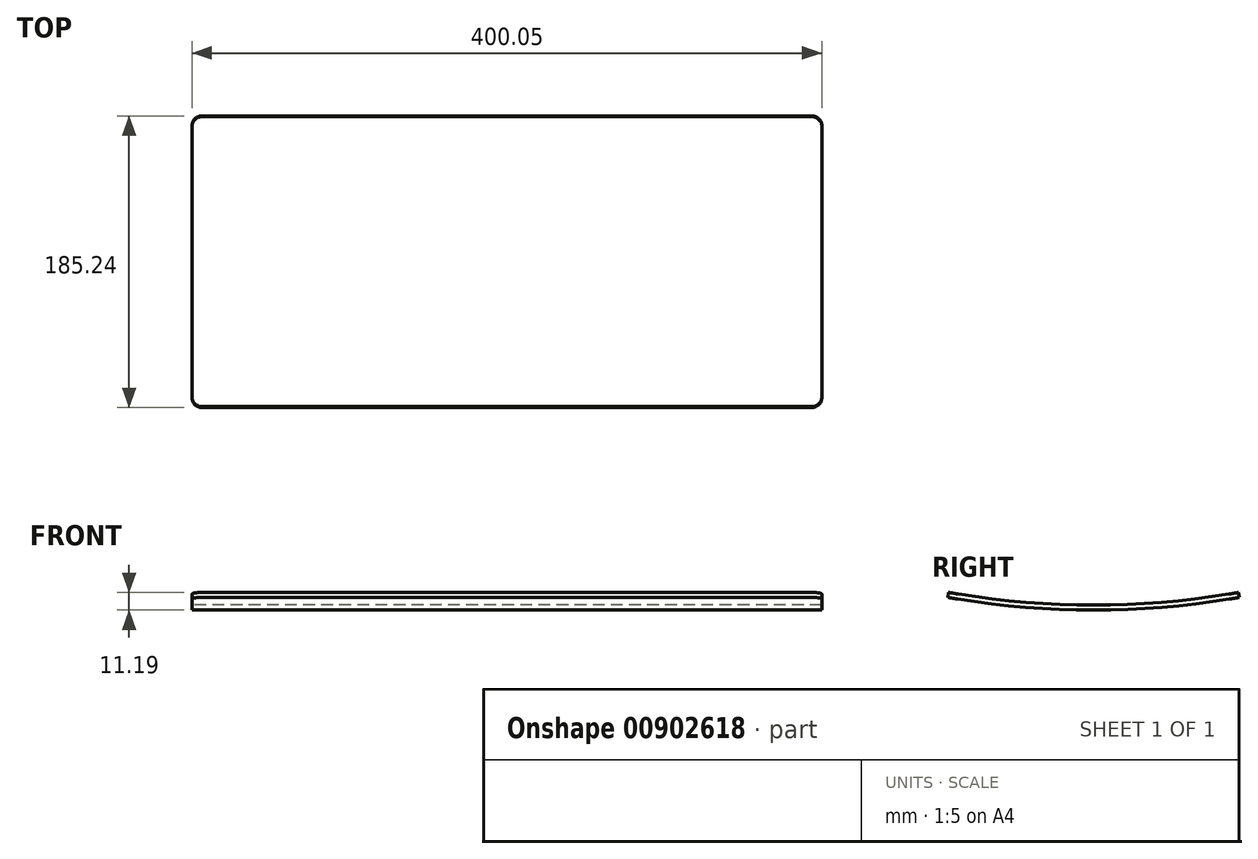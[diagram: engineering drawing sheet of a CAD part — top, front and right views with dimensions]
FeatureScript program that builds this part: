
annotation { "Feature Type Name" : "Feature", "Feature Type Description" : "" }
export const myFeature = defineFeature(function(context is Context, id is Id, definition is map)
    precondition{}
    {
        {
            var Q0;
            Q0=qCreatedBy(makeId("Right.planeOp"),FACE);
            var sketch = newSketch(context, id + "F0", { "sketchPlane" : qUnion([Q0])});
            skArc(sketch, "E0", {"start": v(-76.4, 0) * mm, "mid": v(15.68, -8.02) * mm, "end": v(107.76, 0) * mm});
            skArc(sketch, "E1.0", {"start": v(-76.94, -3.13) * mm, "mid": v(15.68, -11.2) * mm, "end": v(108.3, -3.13) * mm});
            skLineSegment(sketch, "E2", {"start": v(107.76, 0) * mm, "end": v(108.3, -3.13) * mm});
            skLineSegment(sketch, "E3", {"start": v(-76.4, 0) * mm, "end": v(-76.94, -3.13) * mm});
            skSolve(sketch);
        }
        {
            var Q0;
            Q0=qCreatedBy(makeId("Front.planeOp"),FACE);
            var sketch = newSketch(context, id + "F1", { "sketchPlane" : qUnion([Q0])});
            skLineSegment(sketch, "E4", {"start": v(0, 0) * mm, "end": v(-400.05, 0) * mm});
            skSolve(sketch);
        }
        {
            var Q0;
            Q0=makeQuery(id+"F0.imprint","IMPRINT",FACE,{"disambiguationData":[TD([[makeQuery(id+"F0.imprint","IMPRINT",EDGE,{"derivedFrom":sQuery(id+"F0.wireOp",EDGE,"E0")}),-1.0]])]});
            var Q1;
            Q1=sQuery(id+"F1.wireOp",EDGE,"E4");
            sweep(context, id + "F2", {"profiles" : qUnion([Q0]), "path" : qUnion([Q1])});
        }
        {
            var Q0;
            Q0=makeQuery(id+"F2.opSweep","CAP_EDGE",EDGE,{"disambiguationData":[OSD([sQuery(id+"F0.wireOp",EDGE,"E3"),sQuery(id+"F1.wireOp",VERTEX,"E4.end")])],"isStart":false});
            fillet(context, id + "F3", {"entities" : qUnion([Q0]), "radius" : 6.35 * mm, "tangentPropagation" : true, "allowEdgeOverflow" : false});
        }
        {
            var Q0;
            Q0=makeQuery(id+"F2.opSweep","CAP_EDGE",EDGE,{"disambiguationData":[OSD([sQuery(id+"F0.wireOp",EDGE,"E2"),sQuery(id+"F1.wireOp",VERTEX,"E4.end")])],"isStart":false});
            var Q1;
            Q1=makeQuery(id+"F2.opSweep","CAP_EDGE",EDGE,{"disambiguationData":[OSD([sQuery(id+"F0.wireOp",EDGE,"E2"),sQuery(id+"F1.wireOp",VERTEX,"E4.start")])],"isStart":true});
            fillet(context, id + "F4", {"entities" : qUnion([Q0, Q1]), "radius" : 6.35 * mm, "tangentPropagation" : true, "allowEdgeOverflow" : false});
        }
        {
            var Q0;
            Q0=makeQuery(id+"F2.opSweep","CAP_EDGE",EDGE,{"disambiguationData":[OSD([sQuery(id+"F0.wireOp",EDGE,"E3"),sQuery(id+"F1.wireOp",VERTEX,"E4.start")])],"isStart":true});
            fillet(context, id + "F5", {"entities" : qUnion([Q0]), "radius" : 6.35 * mm, "tangentPropagation" : true, "allowEdgeOverflow" : false});
        }
    });
